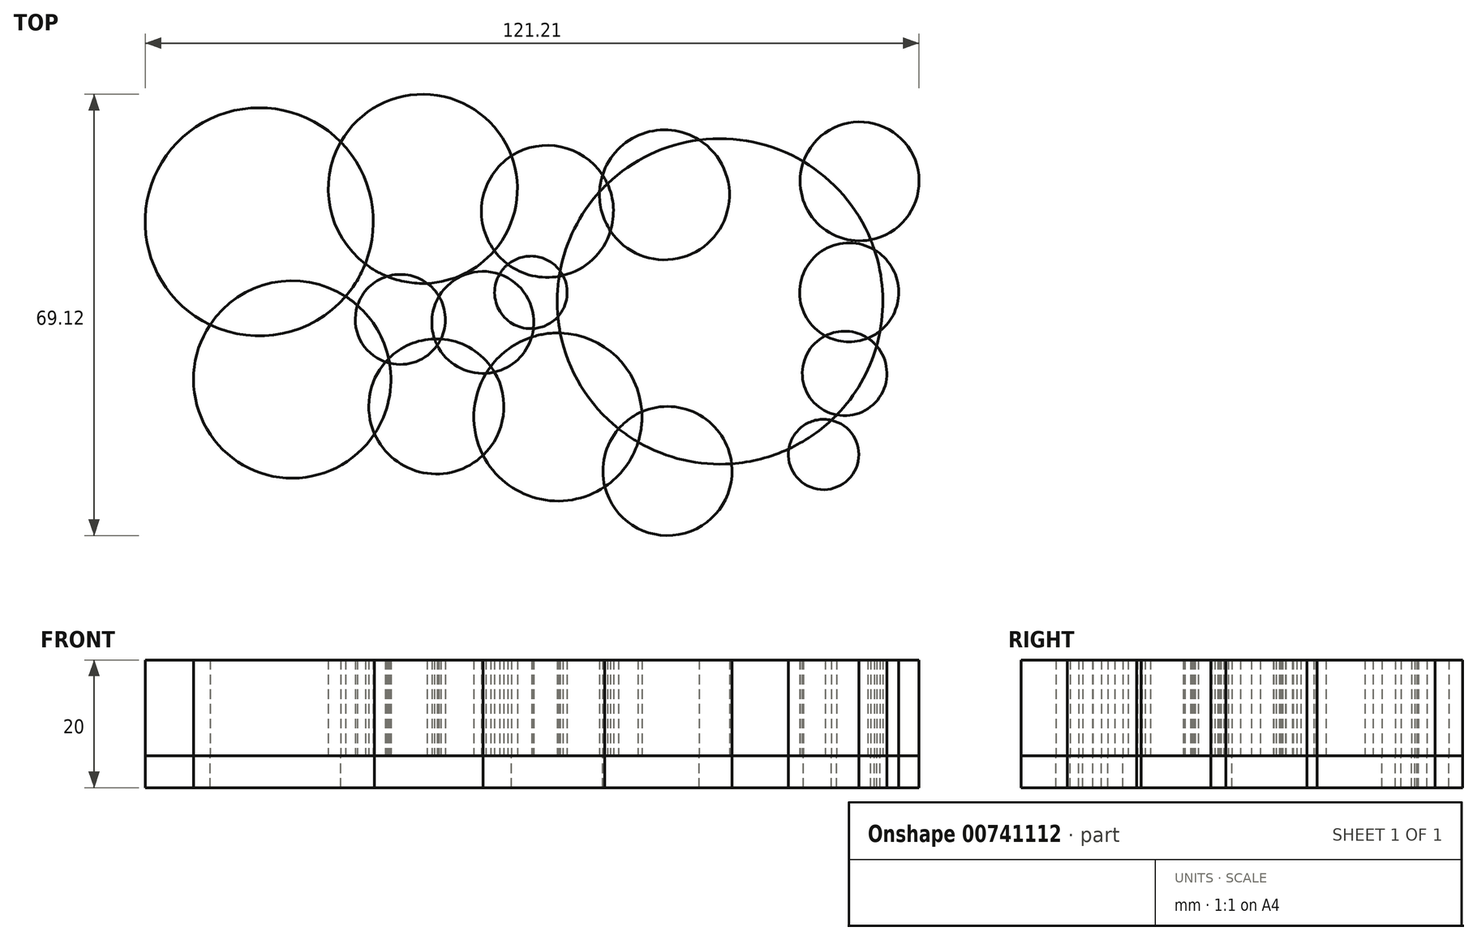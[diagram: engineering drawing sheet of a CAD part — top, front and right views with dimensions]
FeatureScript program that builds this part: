
annotation { "Feature Type Name" : "Feature", "Feature Type Description" : "" }
export const myFeature = defineFeature(function(context is Context, id is Id, definition is map)
    precondition{}
    {
        {
            var Q0;
            Q0=qCreatedBy(makeId("Top.planeOp"),FACE);
            var sketch = newSketch(context, id + "F0", { "sketchPlane" : qUnion([Q0])});
            skCircle(sketch, "E0", {"center": v(-48.84, 19.8) * mm, "radius": 17.87 * mm});
            skCircle(sketch, "E1", {"center": v(-23.21, 24.98) * mm, "radius": 14.8 * mm});
            skCircle(sketch, "E2", {"center": v(-26.74, 4.53) * mm, "radius": 7.05 * mm});
            skCircle(sketch, "E3", {"center": v(-43.67, -4.88) * mm, "radius": 15.46 * mm});
            skCircle(sketch, "E4", {"center": v(-6.29, 8.76) * mm, "radius": 5.68 * mm});
            skCircle(sketch, "E5", {"center": v(-13.81, 4.06) * mm, "radius": 8 * mm});
            skCircle(sketch, "E6", {"center": v(-21.1, -9.1) * mm, "radius": 10.58 * mm});
            skCircle(sketch, "E7", {"center": v(23.33, 7.35) * mm, "radius": 25.5 * mm});
            skCircle(sketch, "E8", {"center": v(-3.7, 21.45) * mm, "radius": 10.34 * mm});
            skCircle(sketch, "E9", {"center": v(-2.06, -10.75) * mm, "radius": 13.16 * mm});
            skCircle(sketch, "E10", {"center": v(45.2, 26.15) * mm, "radius": 9.31 * mm});
            skCircle(sketch, "E11", {"center": v(39.55, -16.63) * mm, "radius": 5.5 * mm});
            skCircle(sketch, "E12", {"center": v(15.1, -19.22) * mm, "radius": 10.11 * mm});
            skCircle(sketch, "E13", {"center": v(14.63, 24.04) * mm, "radius": 10.18 * mm});
            skCircle(sketch, "E14", {"center": v(43.55, 8.76) * mm, "radius": 7.76 * mm});
            skCircle(sketch, "E15", {"center": v(42.84, -3.94) * mm, "radius": 6.62 * mm});
            skSolve(sketch);
        }
        {
            var Q0;
            {var subQ0=sQuery(id+"F0.wireOp",EDGE,"E3");var subQ1=sQuery(id+"F0.wireOp",EDGE,"E0");var subQ2=makeQuery(id+"F0.imprint","INTERSECT",VERTEX,{"disambiguationData":[OD(0.0)],"derivedFrom":[subQ1,subQ0]});Q0=makeQuery(id+"F0.imprint","IMPRINT",FACE,{"disambiguationData":[TD([[makeQuery(id+"F0.imprint","IMPRINT",EDGE,{"disambiguationData":[TD([[subQ2,1.0]])],"derivedFrom":subQ1}),1.0]])]});}
            var Q1;
            {var subQ0=sQuery(id+"F0.wireOp",EDGE,"E1");var subQ1=sQuery(id+"F0.wireOp",EDGE,"E0");var subQ5=makeQuery(id+"F0.imprint","INTERSECT",VERTEX,{"disambiguationData":[OD(0.0)],"derivedFrom":[subQ1,subQ0]});Q1=makeQuery(id+"F0.imprint","IMPRINT",FACE,{"disambiguationData":[TD([[makeQuery(id+"F0.imprint","IMPRINT",EDGE,{"disambiguationData":[TD([[subQ5,1.0]])],"derivedFrom":subQ1}),-1.0]])]});}
            var Q2;
            {var subQ5=sQuery(id+"F0.wireOp",EDGE,"E8");var subQ6=sQuery(id+"F0.wireOp",EDGE,"E1");var subQ7=makeQuery(id+"F0.imprint","INTERSECT",VERTEX,{"disambiguationData":[OD(0.0)],"derivedFrom":[subQ6,subQ5]});Q2=makeQuery(id+"F0.imprint","IMPRINT",FACE,{"disambiguationData":[TD([[makeQuery(id+"F0.imprint","IMPRINT",EDGE,{"disambiguationData":[TD([[subQ7,1.0]])],"derivedFrom":subQ6}),-1.0]])]});}
            var Q3;
            {var subQ0=sQuery(id+"F0.wireOp",EDGE,"E13");var subQ1=sQuery(id+"F0.wireOp",EDGE,"E7");var subQ2=makeQuery(id+"F0.imprint","INTERSECT",VERTEX,{"disambiguationData":[OD(0.0)],"derivedFrom":[subQ1,subQ0]});Q3=makeQuery(id+"F0.imprint","IMPRINT",FACE,{"disambiguationData":[TD([[makeQuery(id+"F0.imprint","IMPRINT",EDGE,{"disambiguationData":[TD([[subQ2,-1.0]])],"derivedFrom":subQ1}),-1.0]])]});}
            var Q4;
            {var subQ14=sQuery(id+"F0.wireOp",EDGE,"E8");var subQ15=sQuery(id+"F0.wireOp",EDGE,"E4");var subQ16=makeQuery(id+"F0.imprint","INTERSECT",VERTEX,{"disambiguationData":[OD(0.0)],"derivedFrom":[subQ15,subQ14]});Q4=makeQuery(id+"F0.imprint","IMPRINT",FACE,{"disambiguationData":[TD([[makeQuery(id+"F0.imprint","IMPRINT",EDGE,{"disambiguationData":[TD([[subQ16,1.0]])],"derivedFrom":subQ15}),-1.0]])]});}
            var Q5;
            {var subQ0=sQuery(id+"F0.wireOp",EDGE,"E10");var subQ1=sQuery(id+"F0.wireOp",EDGE,"E7");var subQ2=makeQuery(id+"F0.imprint","INTERSECT",VERTEX,{"disambiguationData":[OD(0.0)],"derivedFrom":[subQ1,subQ0]});Q5=makeQuery(id+"F0.imprint","IMPRINT",FACE,{"disambiguationData":[TD([[makeQuery(id+"F0.imprint","IMPRINT",EDGE,{"disambiguationData":[TD([[subQ2,-1.0]])],"derivedFrom":subQ1}),-1.0]])]});}
            var Q6;
            {var subQ0=sQuery(id+"F0.wireOp",EDGE,"E14");var subQ1=sQuery(id+"F0.wireOp",EDGE,"E7");var subQ2=makeQuery(id+"F0.imprint","INTERSECT",VERTEX,{"disambiguationData":[OD(0.0)],"derivedFrom":[subQ1,subQ0]});Q6=makeQuery(id+"F0.imprint","IMPRINT",FACE,{"disambiguationData":[TD([[makeQuery(id+"F0.imprint","IMPRINT",EDGE,{"disambiguationData":[TD([[subQ2,1.0]])],"derivedFrom":subQ1}),-1.0]])]});}
            var Q7;
            {var subQ0=sQuery(id+"F0.wireOp",EDGE,"E15");var subQ1=sQuery(id+"F0.wireOp",EDGE,"E7");var subQ2=makeQuery(id+"F0.imprint","INTERSECT",VERTEX,{"disambiguationData":[OD(0.0)],"derivedFrom":[subQ1,subQ0]});Q7=makeQuery(id+"F0.imprint","IMPRINT",FACE,{"disambiguationData":[TD([[makeQuery(id+"F0.imprint","IMPRINT",EDGE,{"disambiguationData":[TD([[subQ2,-1.0]])],"derivedFrom":subQ1}),-1.0]])]});}
            var Q8;
            {var subQ0=sQuery(id+"F0.wireOp",EDGE,"E15");var subQ1=sQuery(id+"F0.wireOp",EDGE,"E14");var subQ2=makeQuery(id+"F0.imprint","INTERSECT",VERTEX,{"disambiguationData":[OD(0.0)],"derivedFrom":[subQ1,subQ0]});Q8=makeQuery(id+"F0.imprint","IMPRINT",FACE,{"disambiguationData":[TD([[makeQuery(id+"F0.imprint","IMPRINT",EDGE,{"disambiguationData":[TD([[subQ2,-1.0]])],"derivedFrom":subQ1}),1.0]])]});}
            var Q9;
            {var subQ0=sQuery(id+"F0.wireOp",EDGE,"E11");var subQ1=sQuery(id+"F0.wireOp",EDGE,"E7");var subQ2=makeQuery(id+"F0.imprint","INTERSECT",VERTEX,{"disambiguationData":[OD(0.0)],"derivedFrom":[subQ1,subQ0]});Q9=makeQuery(id+"F0.imprint","IMPRINT",FACE,{"disambiguationData":[TD([[makeQuery(id+"F0.imprint","IMPRINT",EDGE,{"disambiguationData":[TD([[subQ2,-1.0]])],"derivedFrom":subQ1}),-1.0]])]});}
            var Q10;
            {var subQ0=sQuery(id+"F0.wireOp",EDGE,"E12");var subQ1=sQuery(id+"F0.wireOp",EDGE,"E7");var subQ2=makeQuery(id+"F0.imprint","INTERSECT",VERTEX,{"disambiguationData":[OD(0.0)],"derivedFrom":[subQ1,subQ0]});Q10=makeQuery(id+"F0.imprint","IMPRINT",FACE,{"disambiguationData":[TD([[makeQuery(id+"F0.imprint","IMPRINT",EDGE,{"disambiguationData":[TD([[subQ2,1.0]])],"derivedFrom":subQ1}),-1.0]])]});}
            var Q11;
            {var subQ0=sQuery(id+"F0.wireOp",EDGE,"E12");var subQ1=sQuery(id+"F0.wireOp",EDGE,"E7");var subQ2=makeQuery(id+"F0.imprint","INTERSECT",VERTEX,{"disambiguationData":[OD(1.0)],"derivedFrom":[subQ1,subQ0]});Q11=makeQuery(id+"F0.imprint","IMPRINT",FACE,{"disambiguationData":[TD([[makeQuery(id+"F0.imprint","IMPRINT",EDGE,{"disambiguationData":[TD([[subQ2,-1.0]])],"derivedFrom":subQ1}),1.0]])]});}
            var Q12;
            {var subQ1=sQuery(id+"F0.wireOp",EDGE,"E5");var subQ7=sQuery(id+"F0.wireOp",EDGE,"E6");var subQ10=makeQuery(id+"F0.imprint","INTERSECT",VERTEX,{"disambiguationData":[OD(1.0)],"derivedFrom":[subQ1,subQ7]});Q12=makeQuery(id+"F0.imprint","IMPRINT",FACE,{"disambiguationData":[TD([[makeQuery(id+"F0.imprint","IMPRINT",EDGE,{"disambiguationData":[TD([[subQ10,-1.0]])],"derivedFrom":subQ1}),-1.0]])]});}
            var Q13;
            {var subQ1=sQuery(id+"F0.wireOp",EDGE,"E3");var subQ6=sQuery(id+"F0.wireOp",EDGE,"E2");var subQ9=makeQuery(id+"F0.imprint","INTERSECT",VERTEX,{"disambiguationData":[OD(1.0)],"derivedFrom":[subQ6,subQ1]});Q13=makeQuery(id+"F0.imprint","IMPRINT",FACE,{"disambiguationData":[TD([[makeQuery(id+"F0.imprint","IMPRINT",EDGE,{"disambiguationData":[TD([[subQ9,-1.0]])],"derivedFrom":subQ6}),-1.0]])]});}
            var Q14;
            {var subQ1=sQuery(id+"F0.wireOp",EDGE,"E2");var subQ7=sQuery(id+"F0.wireOp",EDGE,"E1");var subQ10=makeQuery(id+"F0.imprint","INTERSECT",VERTEX,{"disambiguationData":[OD(0.0)],"derivedFrom":[subQ7,subQ1]});Q14=makeQuery(id+"F0.imprint","IMPRINT",FACE,{"disambiguationData":[TD([[makeQuery(id+"F0.imprint","IMPRINT",EDGE,{"disambiguationData":[TD([[subQ10,-1.0]])],"derivedFrom":subQ7}),-1.0]])]});}
            var Q15;
            {var subQ0=sQuery(id+"F0.wireOp",EDGE,"E3");var subQ1=sQuery(id+"F0.wireOp",EDGE,"E0");var subQ2=makeQuery(id+"F0.imprint","INTERSECT",VERTEX,{"disambiguationData":[OD(0.0)],"derivedFrom":[subQ1,subQ0]});Q15=makeQuery(id+"F0.imprint","IMPRINT",FACE,{"disambiguationData":[TD([[makeQuery(id+"F0.imprint","IMPRINT",EDGE,{"disambiguationData":[TD([[subQ2,-1.0]])],"derivedFrom":subQ1}),-1.0]])]});}
            var Q16;
            {var subQ0=sQuery(id+"F0.wireOp",EDGE,"E6");var subQ1=sQuery(id+"F0.wireOp",EDGE,"E2");var subQ2=makeQuery(id+"F0.imprint","INTERSECT",VERTEX,{"disambiguationData":[OD(0.0)],"derivedFrom":[subQ1,subQ0]});Q16=makeQuery(id+"F0.imprint","IMPRINT",FACE,{"disambiguationData":[TD([[makeQuery(id+"F0.imprint","IMPRINT",EDGE,{"disambiguationData":[TD([[subQ2,-1.0]])],"derivedFrom":subQ1}),1.0]])]});}
            var Q17;
            {var subQ0=sQuery(id+"F0.wireOp",EDGE,"E5");var subQ1=sQuery(id+"F0.wireOp",EDGE,"E2");var subQ2=makeQuery(id+"F0.imprint","INTERSECT",VERTEX,{"disambiguationData":[OD(1.0)],"derivedFrom":[subQ1,subQ0]});Q17=makeQuery(id+"F0.imprint","IMPRINT",FACE,{"disambiguationData":[TD([[makeQuery(id+"F0.imprint","IMPRINT",EDGE,{"disambiguationData":[TD([[subQ2,-1.0]])],"derivedFrom":subQ1}),1.0]])]});}
            var Q18;
            {var subQ0=sQuery(id+"F0.wireOp",EDGE,"E9");var subQ1=sQuery(id+"F0.wireOp",EDGE,"E5");var subQ2=makeQuery(id+"F0.imprint","INTERSECT",VERTEX,{"disambiguationData":[OD(0.0)],"derivedFrom":[subQ1,subQ0]});Q18=makeQuery(id+"F0.imprint","IMPRINT",FACE,{"disambiguationData":[TD([[makeQuery(id+"F0.imprint","IMPRINT",EDGE,{"disambiguationData":[TD([[subQ2,-1.0]])],"derivedFrom":subQ1}),1.0]])]});}
            var Q19;
            {var subQ0=sQuery(id+"F0.wireOp",EDGE,"E5");var subQ5=sQuery(id+"F0.wireOp",EDGE,"E2");var subQ6=makeQuery(id+"F0.imprint","INTERSECT",VERTEX,{"disambiguationData":[OD(0.0)],"derivedFrom":[subQ5,subQ0]});Q19=makeQuery(id+"F0.imprint","IMPRINT",FACE,{"disambiguationData":[TD([[makeQuery(id+"F0.imprint","IMPRINT",EDGE,{"disambiguationData":[TD([[subQ6,1.0]])],"derivedFrom":subQ5}),-1.0]])]});}
            var Q20;
            {var subQ1=sQuery(id+"F0.wireOp",EDGE,"E4");var subQ4=sQuery(id+"F0.wireOp",EDGE,"E8");var subQ5=makeQuery(id+"F0.imprint","INTERSECT",VERTEX,{"disambiguationData":[OD(1.0)],"derivedFrom":[subQ1,subQ4]});Q20=makeQuery(id+"F0.imprint","IMPRINT",FACE,{"disambiguationData":[TD([[makeQuery(id+"F0.imprint","IMPRINT",EDGE,{"disambiguationData":[TD([[subQ5,-1.0]])],"derivedFrom":subQ1}),1.0]])]});}
            var Q21;
            {var subQ0=sQuery(id+"F0.wireOp",EDGE,"E7");var subQ1=sQuery(id+"F0.wireOp",EDGE,"E4");var subQ2=makeQuery(id+"F0.imprint","INTERSECT",VERTEX,{"disambiguationData":[OD(0.0)],"derivedFrom":[subQ1,subQ0]});Q21=makeQuery(id+"F0.imprint","IMPRINT",FACE,{"disambiguationData":[TD([[makeQuery(id+"F0.imprint","IMPRINT",EDGE,{"disambiguationData":[TD([[subQ2,1.0]])],"derivedFrom":subQ1}),1.0]])]});}
            var Q22;
            {var subQ0=sQuery(id+"F0.wireOp",EDGE,"E8");var subQ1=sQuery(id+"F0.wireOp",EDGE,"E7");var subQ2=makeQuery(id+"F0.imprint","INTERSECT",VERTEX,{"disambiguationData":[OD(0.0)],"derivedFrom":[subQ1,subQ0]});Q22=makeQuery(id+"F0.imprint","IMPRINT",FACE,{"disambiguationData":[TD([[makeQuery(id+"F0.imprint","IMPRINT",EDGE,{"disambiguationData":[TD([[subQ2,-1.0]])],"derivedFrom":subQ1}),1.0]])]});}
            var Q23;
            {var subQ0=sQuery(id+"F0.wireOp",EDGE,"E15");var subQ1=sQuery(id+"F0.wireOp",EDGE,"E7");var subQ2=makeQuery(id+"F0.imprint","INTERSECT",VERTEX,{"disambiguationData":[OD(1.0)],"derivedFrom":[subQ1,subQ0]});Q23=makeQuery(id+"F0.imprint","IMPRINT",FACE,{"disambiguationData":[TD([[makeQuery(id+"F0.imprint","IMPRINT",EDGE,{"disambiguationData":[TD([[subQ2,-1.0]])],"derivedFrom":subQ1}),1.0]])]});}
            extrude(context, id + "F1", {"entities" : qUnion([Q0, Q1, Q2, Q3, Q4, Q5, Q6, Q7, Q8, Q9, Q10, Q11, Q12, Q13, Q14, Q15, Q16, Q17, Q18, Q19, Q20, Q21, Q22, Q23]), "depth" : 15 * mm, "offsetDistance" : 25 * mm});
        }
        {
            var Q0;
            {var subQ0=sQuery(id+"F0.wireOp",EDGE,"E3");var subQ1=sQuery(id+"F0.wireOp",EDGE,"E0");var subQ2=makeQuery(id+"F0.imprint","INTERSECT",VERTEX,{"disambiguationData":[OD(0.0)],"derivedFrom":[subQ1,subQ0]});Q0=makeQuery(id+"F0.imprint","IMPRINT",FACE,{"disambiguationData":[TD([[makeQuery(id+"F0.imprint","IMPRINT",EDGE,{"disambiguationData":[TD([[subQ2,-1.0]])],"derivedFrom":subQ1}),-1.0]])]});}
            var Q1;
            {var subQ0=sQuery(id+"F0.wireOp",EDGE,"E3");var subQ1=sQuery(id+"F0.wireOp",EDGE,"E2");var subQ2=makeQuery(id+"F0.imprint","INTERSECT",VERTEX,{"disambiguationData":[OD(0.0)],"derivedFrom":[subQ1,subQ0]});Q1=makeQuery(id+"F0.imprint","IMPRINT",FACE,{"disambiguationData":[TD([[makeQuery(id+"F0.imprint","IMPRINT",EDGE,{"disambiguationData":[TD([[subQ2,-1.0]])],"derivedFrom":subQ1}),1.0]])]});}
            var Q2;
            {var subQ0=sQuery(id+"F0.wireOp",EDGE,"E6");var subQ1=sQuery(id+"F0.wireOp",EDGE,"E2");var subQ2=makeQuery(id+"F0.imprint","INTERSECT",VERTEX,{"disambiguationData":[OD(0.0)],"derivedFrom":[subQ1,subQ0]});Q2=makeQuery(id+"F0.imprint","IMPRINT",FACE,{"disambiguationData":[TD([[makeQuery(id+"F0.imprint","IMPRINT",EDGE,{"disambiguationData":[TD([[subQ2,-1.0]])],"derivedFrom":subQ1}),-1.0]])]});}
            var Q3;
            {var subQ0=sQuery(id+"F0.wireOp",EDGE,"E3");var subQ1=sQuery(id+"F0.wireOp",EDGE,"E0");var subQ2=makeQuery(id+"F0.imprint","INTERSECT",VERTEX,{"disambiguationData":[OD(0.0)],"derivedFrom":[subQ1,subQ0]});Q3=makeQuery(id+"F0.imprint","IMPRINT",FACE,{"disambiguationData":[TD([[makeQuery(id+"F0.imprint","IMPRINT",EDGE,{"disambiguationData":[TD([[subQ2,-1.0]])],"derivedFrom":subQ1}),1.0]])]});}
            var Q4;
            {var subQ0=sQuery(id+"F0.wireOp",EDGE,"E3");var subQ1=sQuery(id+"F0.wireOp",EDGE,"E0");var subQ2=makeQuery(id+"F0.imprint","INTERSECT",VERTEX,{"disambiguationData":[OD(0.0)],"derivedFrom":[subQ1,subQ0]});Q4=makeQuery(id+"F0.imprint","IMPRINT",FACE,{"disambiguationData":[TD([[makeQuery(id+"F0.imprint","IMPRINT",EDGE,{"disambiguationData":[TD([[subQ2,1.0]])],"derivedFrom":subQ1}),1.0]])]});}
            var Q5;
            {var subQ0=sQuery(id+"F0.wireOp",EDGE,"E3");var subQ1=sQuery(id+"F0.wireOp",EDGE,"E0");var subQ2=makeQuery(id+"F0.imprint","INTERSECT",VERTEX,{"disambiguationData":[OD(1.0)],"derivedFrom":[subQ1,subQ0]});Q5=makeQuery(id+"F0.imprint","IMPRINT",FACE,{"disambiguationData":[TD([[makeQuery(id+"F0.imprint","IMPRINT",EDGE,{"disambiguationData":[TD([[subQ2,-1.0]])],"derivedFrom":subQ1}),-1.0]])]});}
            var Q6;
            {var subQ0=sQuery(id+"F0.wireOp",EDGE,"E1");var subQ1=sQuery(id+"F0.wireOp",EDGE,"E0");var subQ2=makeQuery(id+"F0.imprint","INTERSECT",VERTEX,{"disambiguationData":[OD(0.0)],"derivedFrom":[subQ1,subQ0]});Q6=makeQuery(id+"F0.imprint","IMPRINT",FACE,{"disambiguationData":[TD([[makeQuery(id+"F0.imprint","IMPRINT",EDGE,{"disambiguationData":[TD([[subQ2,1.0]])],"derivedFrom":subQ1}),1.0]])]});}
            var Q7;
            {var subQ0=sQuery(id+"F0.wireOp",EDGE,"E1");var subQ1=sQuery(id+"F0.wireOp",EDGE,"E0");var subQ5=makeQuery(id+"F0.imprint","INTERSECT",VERTEX,{"disambiguationData":[OD(0.0)],"derivedFrom":[subQ1,subQ0]});Q7=makeQuery(id+"F0.imprint","IMPRINT",FACE,{"disambiguationData":[TD([[makeQuery(id+"F0.imprint","IMPRINT",EDGE,{"disambiguationData":[TD([[subQ5,1.0]])],"derivedFrom":subQ1}),-1.0]])]});}
            var Q8;
            {var subQ0=sQuery(id+"F0.wireOp",EDGE,"E2");var subQ1=sQuery(id+"F0.wireOp",EDGE,"E1");var subQ2=makeQuery(id+"F0.imprint","INTERSECT",VERTEX,{"disambiguationData":[OD(0.0)],"derivedFrom":[subQ1,subQ0]});Q8=makeQuery(id+"F0.imprint","IMPRINT",FACE,{"disambiguationData":[TD([[makeQuery(id+"F0.imprint","IMPRINT",EDGE,{"disambiguationData":[TD([[subQ2,-1.0]])],"derivedFrom":subQ1}),1.0]])]});}
            var Q9;
            {var subQ0=sQuery(id+"F0.wireOp",EDGE,"E5");var subQ1=sQuery(id+"F0.wireOp",EDGE,"E2");var subQ2=makeQuery(id+"F0.imprint","INTERSECT",VERTEX,{"disambiguationData":[OD(0.0)],"derivedFrom":[subQ1,subQ0]});Q9=makeQuery(id+"F0.imprint","IMPRINT",FACE,{"disambiguationData":[TD([[makeQuery(id+"F0.imprint","IMPRINT",EDGE,{"disambiguationData":[TD([[subQ2,1.0]])],"derivedFrom":subQ1}),1.0]])]});}
            var Q10;
            {var subQ0=sQuery(id+"F0.wireOp",EDGE,"E3");var subQ1=sQuery(id+"F0.wireOp",EDGE,"E2");var subQ2=makeQuery(id+"F0.imprint","INTERSECT",VERTEX,{"disambiguationData":[OD(1.0)],"derivedFrom":[subQ1,subQ0]});Q10=makeQuery(id+"F0.imprint","IMPRINT",FACE,{"disambiguationData":[TD([[makeQuery(id+"F0.imprint","IMPRINT",EDGE,{"disambiguationData":[TD([[subQ2,-1.0]])],"derivedFrom":subQ1}),1.0]])]});}
            var Q11;
            {var subQ0=sQuery(id+"F0.wireOp",EDGE,"E6");var subQ1=sQuery(id+"F0.wireOp",EDGE,"E2");var subQ2=makeQuery(id+"F0.imprint","INTERSECT",VERTEX,{"disambiguationData":[OD(0.0)],"derivedFrom":[subQ1,subQ0]});Q11=makeQuery(id+"F0.imprint","IMPRINT",FACE,{"disambiguationData":[TD([[makeQuery(id+"F0.imprint","IMPRINT",EDGE,{"disambiguationData":[TD([[subQ2,-1.0]])],"derivedFrom":subQ1}),1.0]])]});}
            var Q12;
            {var subQ0=sQuery(id+"F0.wireOp",EDGE,"E5");var subQ1=sQuery(id+"F0.wireOp",EDGE,"E2");var subQ2=makeQuery(id+"F0.imprint","INTERSECT",VERTEX,{"disambiguationData":[OD(1.0)],"derivedFrom":[subQ1,subQ0]});Q12=makeQuery(id+"F0.imprint","IMPRINT",FACE,{"disambiguationData":[TD([[makeQuery(id+"F0.imprint","IMPRINT",EDGE,{"disambiguationData":[TD([[subQ2,-1.0]])],"derivedFrom":subQ1}),1.0]])]});}
            var Q13;
            {var subQ1=sQuery(id+"F0.wireOp",EDGE,"E3");var subQ6=sQuery(id+"F0.wireOp",EDGE,"E2");var subQ9=makeQuery(id+"F0.imprint","INTERSECT",VERTEX,{"disambiguationData":[OD(1.0)],"derivedFrom":[subQ6,subQ1]});Q13=makeQuery(id+"F0.imprint","IMPRINT",FACE,{"disambiguationData":[TD([[makeQuery(id+"F0.imprint","IMPRINT",EDGE,{"disambiguationData":[TD([[subQ9,-1.0]])],"derivedFrom":subQ6}),-1.0]])]});}
            var Q14;
            {var subQ0=sQuery(id+"F0.wireOp",EDGE,"E5");var subQ1=sQuery(id+"F0.wireOp",EDGE,"E2");var subQ2=makeQuery(id+"F0.imprint","INTERSECT",VERTEX,{"disambiguationData":[OD(1.0)],"derivedFrom":[subQ1,subQ0]});Q14=makeQuery(id+"F0.imprint","IMPRINT",FACE,{"disambiguationData":[TD([[makeQuery(id+"F0.imprint","IMPRINT",EDGE,{"disambiguationData":[TD([[subQ2,-1.0]])],"derivedFrom":subQ1}),-1.0]])]});}
            var Q15;
            {var subQ0=sQuery(id+"F0.wireOp",EDGE,"E5");var subQ5=sQuery(id+"F0.wireOp",EDGE,"E2");var subQ6=makeQuery(id+"F0.imprint","INTERSECT",VERTEX,{"disambiguationData":[OD(0.0)],"derivedFrom":[subQ5,subQ0]});Q15=makeQuery(id+"F0.imprint","IMPRINT",FACE,{"disambiguationData":[TD([[makeQuery(id+"F0.imprint","IMPRINT",EDGE,{"disambiguationData":[TD([[subQ6,1.0]])],"derivedFrom":subQ5}),-1.0]])]});}
            var Q16;
            {var subQ5=sQuery(id+"F0.wireOp",EDGE,"E2");var subQ7=sQuery(id+"F0.wireOp",EDGE,"E1");var subQ8=makeQuery(id+"F0.imprint","INTERSECT",VERTEX,{"disambiguationData":[OD(1.0)],"derivedFrom":[subQ7,subQ5]});Q16=makeQuery(id+"F0.imprint","IMPRINT",FACE,{"disambiguationData":[TD([[makeQuery(id+"F0.imprint","IMPRINT",EDGE,{"disambiguationData":[TD([[subQ8,-1.0]])],"derivedFrom":subQ7}),-1.0]])]});}
            var Q17;
            {var subQ0=sQuery(id+"F0.wireOp",EDGE,"E8");var subQ1=sQuery(id+"F0.wireOp",EDGE,"E1");var subQ2=makeQuery(id+"F0.imprint","INTERSECT",VERTEX,{"disambiguationData":[OD(0.0)],"derivedFrom":[subQ1,subQ0]});Q17=makeQuery(id+"F0.imprint","IMPRINT",FACE,{"disambiguationData":[TD([[makeQuery(id+"F0.imprint","IMPRINT",EDGE,{"disambiguationData":[TD([[subQ2,1.0]])],"derivedFrom":subQ1}),1.0]])]});}
            var Q18;
            {var subQ5=sQuery(id+"F0.wireOp",EDGE,"E8");var subQ6=sQuery(id+"F0.wireOp",EDGE,"E1");var subQ7=makeQuery(id+"F0.imprint","INTERSECT",VERTEX,{"disambiguationData":[OD(0.0)],"derivedFrom":[subQ6,subQ5]});Q18=makeQuery(id+"F0.imprint","IMPRINT",FACE,{"disambiguationData":[TD([[makeQuery(id+"F0.imprint","IMPRINT",EDGE,{"disambiguationData":[TD([[subQ7,1.0]])],"derivedFrom":subQ6}),-1.0]])]});}
            var Q19;
            {var subQ0=sQuery(id+"F0.wireOp",EDGE,"E7");var subQ1=sQuery(id+"F0.wireOp",EDGE,"E4");var subQ2=makeQuery(id+"F0.imprint","INTERSECT",VERTEX,{"disambiguationData":[OD(0.0)],"derivedFrom":[subQ1,subQ0]});Q19=makeQuery(id+"F0.imprint","IMPRINT",FACE,{"disambiguationData":[TD([[makeQuery(id+"F0.imprint","IMPRINT",EDGE,{"disambiguationData":[TD([[subQ2,-1.0]])],"derivedFrom":subQ1}),1.0]])]});}
            var Q20;
            {var subQ0=sQuery(id+"F0.wireOp",EDGE,"E5");var subQ1=sQuery(id+"F0.wireOp",EDGE,"E4");var subQ2=makeQuery(id+"F0.imprint","INTERSECT",VERTEX,{"disambiguationData":[OD(0.0)],"derivedFrom":[subQ1,subQ0]});Q20=makeQuery(id+"F0.imprint","IMPRINT",FACE,{"disambiguationData":[TD([[makeQuery(id+"F0.imprint","IMPRINT",EDGE,{"disambiguationData":[TD([[subQ2,-1.0]])],"derivedFrom":subQ1}),1.0]])]});}
            var Q21;
            {var subQ1=sQuery(id+"F0.wireOp",EDGE,"E4");var subQ4=sQuery(id+"F0.wireOp",EDGE,"E8");var subQ5=makeQuery(id+"F0.imprint","INTERSECT",VERTEX,{"disambiguationData":[OD(1.0)],"derivedFrom":[subQ1,subQ4]});Q21=makeQuery(id+"F0.imprint","IMPRINT",FACE,{"disambiguationData":[TD([[makeQuery(id+"F0.imprint","IMPRINT",EDGE,{"disambiguationData":[TD([[subQ5,-1.0]])],"derivedFrom":subQ1}),1.0]])]});}
            var Q22;
            {var subQ0=sQuery(id+"F0.wireOp",EDGE,"E6");var subQ1=sQuery(id+"F0.wireOp",EDGE,"E5");var subQ2=makeQuery(id+"F0.imprint","INTERSECT",VERTEX,{"disambiguationData":[OD(1.0)],"derivedFrom":[subQ1,subQ0]});Q22=makeQuery(id+"F0.imprint","IMPRINT",FACE,{"disambiguationData":[TD([[makeQuery(id+"F0.imprint","IMPRINT",EDGE,{"disambiguationData":[TD([[subQ2,-1.0]])],"derivedFrom":subQ1}),1.0]])]});}
            var Q23;
            {var subQ0=sQuery(id+"F0.wireOp",EDGE,"E9");var subQ1=sQuery(id+"F0.wireOp",EDGE,"E5");var subQ2=makeQuery(id+"F0.imprint","INTERSECT",VERTEX,{"disambiguationData":[OD(0.0)],"derivedFrom":[subQ1,subQ0]});Q23=makeQuery(id+"F0.imprint","IMPRINT",FACE,{"disambiguationData":[TD([[makeQuery(id+"F0.imprint","IMPRINT",EDGE,{"disambiguationData":[TD([[subQ2,-1.0]])],"derivedFrom":subQ1}),-1.0]])]});}
            var Q24;
            {var subQ1=sQuery(id+"F0.wireOp",EDGE,"E5");var subQ7=sQuery(id+"F0.wireOp",EDGE,"E6");var subQ10=makeQuery(id+"F0.imprint","INTERSECT",VERTEX,{"disambiguationData":[OD(1.0)],"derivedFrom":[subQ1,subQ7]});Q24=makeQuery(id+"F0.imprint","IMPRINT",FACE,{"disambiguationData":[TD([[makeQuery(id+"F0.imprint","IMPRINT",EDGE,{"disambiguationData":[TD([[subQ10,-1.0]])],"derivedFrom":subQ1}),-1.0]])]});}
            var Q25;
            {var subQ1=sQuery(id+"F0.wireOp",EDGE,"E2");var subQ7=sQuery(id+"F0.wireOp",EDGE,"E1");var subQ10=makeQuery(id+"F0.imprint","INTERSECT",VERTEX,{"disambiguationData":[OD(0.0)],"derivedFrom":[subQ7,subQ1]});Q25=makeQuery(id+"F0.imprint","IMPRINT",FACE,{"disambiguationData":[TD([[makeQuery(id+"F0.imprint","IMPRINT",EDGE,{"disambiguationData":[TD([[subQ10,-1.0]])],"derivedFrom":subQ7}),-1.0]])]});}
            var Q26;
            {var subQ0=sQuery(id+"F0.wireOp",EDGE,"E9");var subQ1=sQuery(id+"F0.wireOp",EDGE,"E5");var subQ2=makeQuery(id+"F0.imprint","INTERSECT",VERTEX,{"disambiguationData":[OD(0.0)],"derivedFrom":[subQ1,subQ0]});Q26=makeQuery(id+"F0.imprint","IMPRINT",FACE,{"disambiguationData":[TD([[makeQuery(id+"F0.imprint","IMPRINT",EDGE,{"disambiguationData":[TD([[subQ2,-1.0]])],"derivedFrom":subQ1}),1.0]])]});}
            var Q27;
            {var subQ0=sQuery(id+"F0.wireOp",EDGE,"E9");var subQ1=sQuery(id+"F0.wireOp",EDGE,"E7");var subQ2=makeQuery(id+"F0.imprint","INTERSECT",VERTEX,{"disambiguationData":[OD(0.0)],"derivedFrom":[subQ1,subQ0]});Q27=makeQuery(id+"F0.imprint","IMPRINT",FACE,{"disambiguationData":[TD([[makeQuery(id+"F0.imprint","IMPRINT",EDGE,{"disambiguationData":[TD([[subQ2,-1.0]])],"derivedFrom":subQ1}),1.0]])]});}
            var Q28;
            {var subQ0=sQuery(id+"F0.wireOp",EDGE,"E5");var subQ1=sQuery(id+"F0.wireOp",EDGE,"E4");var subQ2=makeQuery(id+"F0.imprint","INTERSECT",VERTEX,{"disambiguationData":[OD(1.0)],"derivedFrom":[subQ1,subQ0]});Q28=makeQuery(id+"F0.imprint","IMPRINT",FACE,{"disambiguationData":[TD([[makeQuery(id+"F0.imprint","IMPRINT",EDGE,{"disambiguationData":[TD([[subQ2,-1.0]])],"derivedFrom":subQ1}),-1.0]])]});}
            var Q29;
            {var subQ0=sQuery(id+"F0.wireOp",EDGE,"E8");var subQ1=sQuery(id+"F0.wireOp",EDGE,"E4");var subQ2=makeQuery(id+"F0.imprint","INTERSECT",VERTEX,{"disambiguationData":[OD(0.0)],"derivedFrom":[subQ1,subQ0]});Q29=makeQuery(id+"F0.imprint","IMPRINT",FACE,{"disambiguationData":[TD([[makeQuery(id+"F0.imprint","IMPRINT",EDGE,{"disambiguationData":[TD([[subQ2,1.0]])],"derivedFrom":subQ1}),1.0]])]});}
            var Q30;
            {var subQ14=sQuery(id+"F0.wireOp",EDGE,"E8");var subQ15=sQuery(id+"F0.wireOp",EDGE,"E4");var subQ16=makeQuery(id+"F0.imprint","INTERSECT",VERTEX,{"disambiguationData":[OD(0.0)],"derivedFrom":[subQ15,subQ14]});Q30=makeQuery(id+"F0.imprint","IMPRINT",FACE,{"disambiguationData":[TD([[makeQuery(id+"F0.imprint","IMPRINT",EDGE,{"disambiguationData":[TD([[subQ16,1.0]])],"derivedFrom":subQ15}),-1.0]])]});}
            var Q31;
            {var subQ0=sQuery(id+"F0.wireOp",EDGE,"E13");var subQ1=sQuery(id+"F0.wireOp",EDGE,"E7");var subQ2=makeQuery(id+"F0.imprint","INTERSECT",VERTEX,{"disambiguationData":[OD(0.0)],"derivedFrom":[subQ1,subQ0]});Q31=makeQuery(id+"F0.imprint","IMPRINT",FACE,{"disambiguationData":[TD([[makeQuery(id+"F0.imprint","IMPRINT",EDGE,{"disambiguationData":[TD([[subQ2,-1.0]])],"derivedFrom":subQ1}),1.0]])]});}
            var Q32;
            {var subQ0=sQuery(id+"F0.wireOp",EDGE,"E8");var subQ1=sQuery(id+"F0.wireOp",EDGE,"E7");var subQ2=makeQuery(id+"F0.imprint","INTERSECT",VERTEX,{"disambiguationData":[OD(0.0)],"derivedFrom":[subQ1,subQ0]});Q32=makeQuery(id+"F0.imprint","IMPRINT",FACE,{"disambiguationData":[TD([[makeQuery(id+"F0.imprint","IMPRINT",EDGE,{"disambiguationData":[TD([[subQ2,-1.0]])],"derivedFrom":subQ1}),-1.0]])]});}
            var Q33;
            {var subQ0=sQuery(id+"F0.wireOp",EDGE,"E8");var subQ1=sQuery(id+"F0.wireOp",EDGE,"E7");var subQ2=makeQuery(id+"F0.imprint","INTERSECT",VERTEX,{"disambiguationData":[OD(0.0)],"derivedFrom":[subQ1,subQ0]});Q33=makeQuery(id+"F0.imprint","IMPRINT",FACE,{"disambiguationData":[TD([[makeQuery(id+"F0.imprint","IMPRINT",EDGE,{"disambiguationData":[TD([[subQ2,-1.0]])],"derivedFrom":subQ1}),1.0]])]});}
            var Q34;
            {var subQ0=sQuery(id+"F0.wireOp",EDGE,"E7");var subQ1=sQuery(id+"F0.wireOp",EDGE,"E4");var subQ2=makeQuery(id+"F0.imprint","INTERSECT",VERTEX,{"disambiguationData":[OD(0.0)],"derivedFrom":[subQ1,subQ0]});Q34=makeQuery(id+"F0.imprint","IMPRINT",FACE,{"disambiguationData":[TD([[makeQuery(id+"F0.imprint","IMPRINT",EDGE,{"disambiguationData":[TD([[subQ2,1.0]])],"derivedFrom":subQ1}),-1.0]])]});}
            var Q35;
            {var subQ0=sQuery(id+"F0.wireOp",EDGE,"E7");var subQ1=sQuery(id+"F0.wireOp",EDGE,"E4");var subQ2=makeQuery(id+"F0.imprint","INTERSECT",VERTEX,{"disambiguationData":[OD(0.0)],"derivedFrom":[subQ1,subQ0]});Q35=makeQuery(id+"F0.imprint","IMPRINT",FACE,{"disambiguationData":[TD([[makeQuery(id+"F0.imprint","IMPRINT",EDGE,{"disambiguationData":[TD([[subQ2,1.0]])],"derivedFrom":subQ1}),1.0]])]});}
            var Q36;
            {var subQ0=sQuery(id+"F0.wireOp",EDGE,"E13");var subQ1=sQuery(id+"F0.wireOp",EDGE,"E7");var subQ2=makeQuery(id+"F0.imprint","INTERSECT",VERTEX,{"disambiguationData":[OD(0.0)],"derivedFrom":[subQ1,subQ0]});Q36=makeQuery(id+"F0.imprint","IMPRINT",FACE,{"disambiguationData":[TD([[makeQuery(id+"F0.imprint","IMPRINT",EDGE,{"disambiguationData":[TD([[subQ2,-1.0]])],"derivedFrom":subQ1}),-1.0]])]});}
            var Q37;
            {var subQ0=sQuery(id+"F0.wireOp",EDGE,"E10");var subQ1=sQuery(id+"F0.wireOp",EDGE,"E7");var subQ2=makeQuery(id+"F0.imprint","INTERSECT",VERTEX,{"disambiguationData":[OD(0.0)],"derivedFrom":[subQ1,subQ0]});Q37=makeQuery(id+"F0.imprint","IMPRINT",FACE,{"disambiguationData":[TD([[makeQuery(id+"F0.imprint","IMPRINT",EDGE,{"disambiguationData":[TD([[subQ2,-1.0]])],"derivedFrom":subQ1}),1.0]])]});}
            var Q38;
            {var subQ0=sQuery(id+"F0.wireOp",EDGE,"E10");var subQ1=sQuery(id+"F0.wireOp",EDGE,"E7");var subQ2=makeQuery(id+"F0.imprint","INTERSECT",VERTEX,{"disambiguationData":[OD(0.0)],"derivedFrom":[subQ1,subQ0]});Q38=makeQuery(id+"F0.imprint","IMPRINT",FACE,{"disambiguationData":[TD([[makeQuery(id+"F0.imprint","IMPRINT",EDGE,{"disambiguationData":[TD([[subQ2,-1.0]])],"derivedFrom":subQ1}),-1.0]])]});}
            var Q39;
            {var subQ0=sQuery(id+"F0.wireOp",EDGE,"E14");var subQ1=sQuery(id+"F0.wireOp",EDGE,"E7");var subQ2=makeQuery(id+"F0.imprint","INTERSECT",VERTEX,{"disambiguationData":[OD(0.0)],"derivedFrom":[subQ1,subQ0]});Q39=makeQuery(id+"F0.imprint","IMPRINT",FACE,{"disambiguationData":[TD([[makeQuery(id+"F0.imprint","IMPRINT",EDGE,{"disambiguationData":[TD([[subQ2,1.0]])],"derivedFrom":subQ1}),1.0]])]});}
            var Q40;
            {var subQ0=sQuery(id+"F0.wireOp",EDGE,"E14");var subQ1=sQuery(id+"F0.wireOp",EDGE,"E7");var subQ2=makeQuery(id+"F0.imprint","INTERSECT",VERTEX,{"disambiguationData":[OD(0.0)],"derivedFrom":[subQ1,subQ0]});Q40=makeQuery(id+"F0.imprint","IMPRINT",FACE,{"disambiguationData":[TD([[makeQuery(id+"F0.imprint","IMPRINT",EDGE,{"disambiguationData":[TD([[subQ2,1.0]])],"derivedFrom":subQ1}),-1.0]])]});}
            var Q41;
            {var subQ0=sQuery(id+"F0.wireOp",EDGE,"E15");var subQ1=sQuery(id+"F0.wireOp",EDGE,"E14");var subQ2=makeQuery(id+"F0.imprint","INTERSECT",VERTEX,{"disambiguationData":[OD(0.0)],"derivedFrom":[subQ1,subQ0]});Q41=makeQuery(id+"F0.imprint","IMPRINT",FACE,{"disambiguationData":[TD([[makeQuery(id+"F0.imprint","IMPRINT",EDGE,{"disambiguationData":[TD([[subQ2,-1.0]])],"derivedFrom":subQ1}),1.0]])]});}
            var Q42;
            {var subQ0=sQuery(id+"F0.wireOp",EDGE,"E15");var subQ1=sQuery(id+"F0.wireOp",EDGE,"E7");var subQ2=makeQuery(id+"F0.imprint","INTERSECT",VERTEX,{"disambiguationData":[OD(1.0)],"derivedFrom":[subQ1,subQ0]});Q42=makeQuery(id+"F0.imprint","IMPRINT",FACE,{"disambiguationData":[TD([[makeQuery(id+"F0.imprint","IMPRINT",EDGE,{"disambiguationData":[TD([[subQ2,-1.0]])],"derivedFrom":subQ1}),1.0]])]});}
            var Q43;
            {var subQ0=sQuery(id+"F0.wireOp",EDGE,"E15");var subQ1=sQuery(id+"F0.wireOp",EDGE,"E7");var subQ2=makeQuery(id+"F0.imprint","INTERSECT",VERTEX,{"disambiguationData":[OD(0.0)],"derivedFrom":[subQ1,subQ0]});Q43=makeQuery(id+"F0.imprint","IMPRINT",FACE,{"disambiguationData":[TD([[makeQuery(id+"F0.imprint","IMPRINT",EDGE,{"disambiguationData":[TD([[subQ2,-1.0]])],"derivedFrom":subQ1}),1.0]])]});}
            var Q44;
            {var subQ0=sQuery(id+"F0.wireOp",EDGE,"E15");var subQ1=sQuery(id+"F0.wireOp",EDGE,"E7");var subQ2=makeQuery(id+"F0.imprint","INTERSECT",VERTEX,{"disambiguationData":[OD(0.0)],"derivedFrom":[subQ1,subQ0]});Q44=makeQuery(id+"F0.imprint","IMPRINT",FACE,{"disambiguationData":[TD([[makeQuery(id+"F0.imprint","IMPRINT",EDGE,{"disambiguationData":[TD([[subQ2,-1.0]])],"derivedFrom":subQ1}),-1.0]])]});}
            var Q45;
            {var subQ0=sQuery(id+"F0.wireOp",EDGE,"E11");var subQ1=sQuery(id+"F0.wireOp",EDGE,"E7");var subQ2=makeQuery(id+"F0.imprint","INTERSECT",VERTEX,{"disambiguationData":[OD(0.0)],"derivedFrom":[subQ1,subQ0]});Q45=makeQuery(id+"F0.imprint","IMPRINT",FACE,{"disambiguationData":[TD([[makeQuery(id+"F0.imprint","IMPRINT",EDGE,{"disambiguationData":[TD([[subQ2,-1.0]])],"derivedFrom":subQ1}),1.0]])]});}
            var Q46;
            {var subQ0=sQuery(id+"F0.wireOp",EDGE,"E11");var subQ1=sQuery(id+"F0.wireOp",EDGE,"E7");var subQ2=makeQuery(id+"F0.imprint","INTERSECT",VERTEX,{"disambiguationData":[OD(0.0)],"derivedFrom":[subQ1,subQ0]});Q46=makeQuery(id+"F0.imprint","IMPRINT",FACE,{"disambiguationData":[TD([[makeQuery(id+"F0.imprint","IMPRINT",EDGE,{"disambiguationData":[TD([[subQ2,-1.0]])],"derivedFrom":subQ1}),-1.0]])]});}
            var Q47;
            {var subQ0=sQuery(id+"F0.wireOp",EDGE,"E12");var subQ1=sQuery(id+"F0.wireOp",EDGE,"E7");var subQ2=makeQuery(id+"F0.imprint","INTERSECT",VERTEX,{"disambiguationData":[OD(0.0)],"derivedFrom":[subQ1,subQ0]});Q47=makeQuery(id+"F0.imprint","IMPRINT",FACE,{"disambiguationData":[TD([[makeQuery(id+"F0.imprint","IMPRINT",EDGE,{"disambiguationData":[TD([[subQ2,1.0]])],"derivedFrom":subQ1}),1.0]])]});}
            var Q48;
            {var subQ0=sQuery(id+"F0.wireOp",EDGE,"E12");var subQ1=sQuery(id+"F0.wireOp",EDGE,"E7");var subQ2=makeQuery(id+"F0.imprint","INTERSECT",VERTEX,{"disambiguationData":[OD(1.0)],"derivedFrom":[subQ1,subQ0]});Q48=makeQuery(id+"F0.imprint","IMPRINT",FACE,{"disambiguationData":[TD([[makeQuery(id+"F0.imprint","IMPRINT",EDGE,{"disambiguationData":[TD([[subQ2,-1.0]])],"derivedFrom":subQ1}),1.0]])]});}
            var Q49;
            {var subQ0=sQuery(id+"F0.wireOp",EDGE,"E12");var subQ1=sQuery(id+"F0.wireOp",EDGE,"E7");var subQ2=makeQuery(id+"F0.imprint","INTERSECT",VERTEX,{"disambiguationData":[OD(1.0)],"derivedFrom":[subQ1,subQ0]});Q49=makeQuery(id+"F0.imprint","IMPRINT",FACE,{"disambiguationData":[TD([[makeQuery(id+"F0.imprint","IMPRINT",EDGE,{"disambiguationData":[TD([[subQ2,-1.0]])],"derivedFrom":subQ1}),-1.0]])]});}
            var Q50;
            {var subQ0=sQuery(id+"F0.wireOp",EDGE,"E12");var subQ1=sQuery(id+"F0.wireOp",EDGE,"E7");var subQ2=makeQuery(id+"F0.imprint","INTERSECT",VERTEX,{"disambiguationData":[OD(0.0)],"derivedFrom":[subQ1,subQ0]});Q50=makeQuery(id+"F0.imprint","IMPRINT",FACE,{"disambiguationData":[TD([[makeQuery(id+"F0.imprint","IMPRINT",EDGE,{"disambiguationData":[TD([[subQ2,1.0]])],"derivedFrom":subQ1}),-1.0]])]});}
            extrude(context, id + "F2", {"entities" : qUnion([Q0, Q1, Q2, Q3, Q4, Q5, Q6, Q7, Q8, Q9, Q10, Q11, Q12, Q13, Q14, Q15, Q16, Q17, Q18, Q19, Q20, Q21, Q22, Q23, Q24, Q25, Q26, Q27, Q28, Q29, Q30, Q31, Q32, Q33, Q34, Q35, Q36, Q37, Q38, Q39, Q40, Q41, Q42, Q43, Q44, Q45, Q46, Q47, Q48, Q49, Q50]), "oppositeDirection" : true, "depth" : 5 * mm, "offsetDistance" : 25 * mm});
        }
    });
